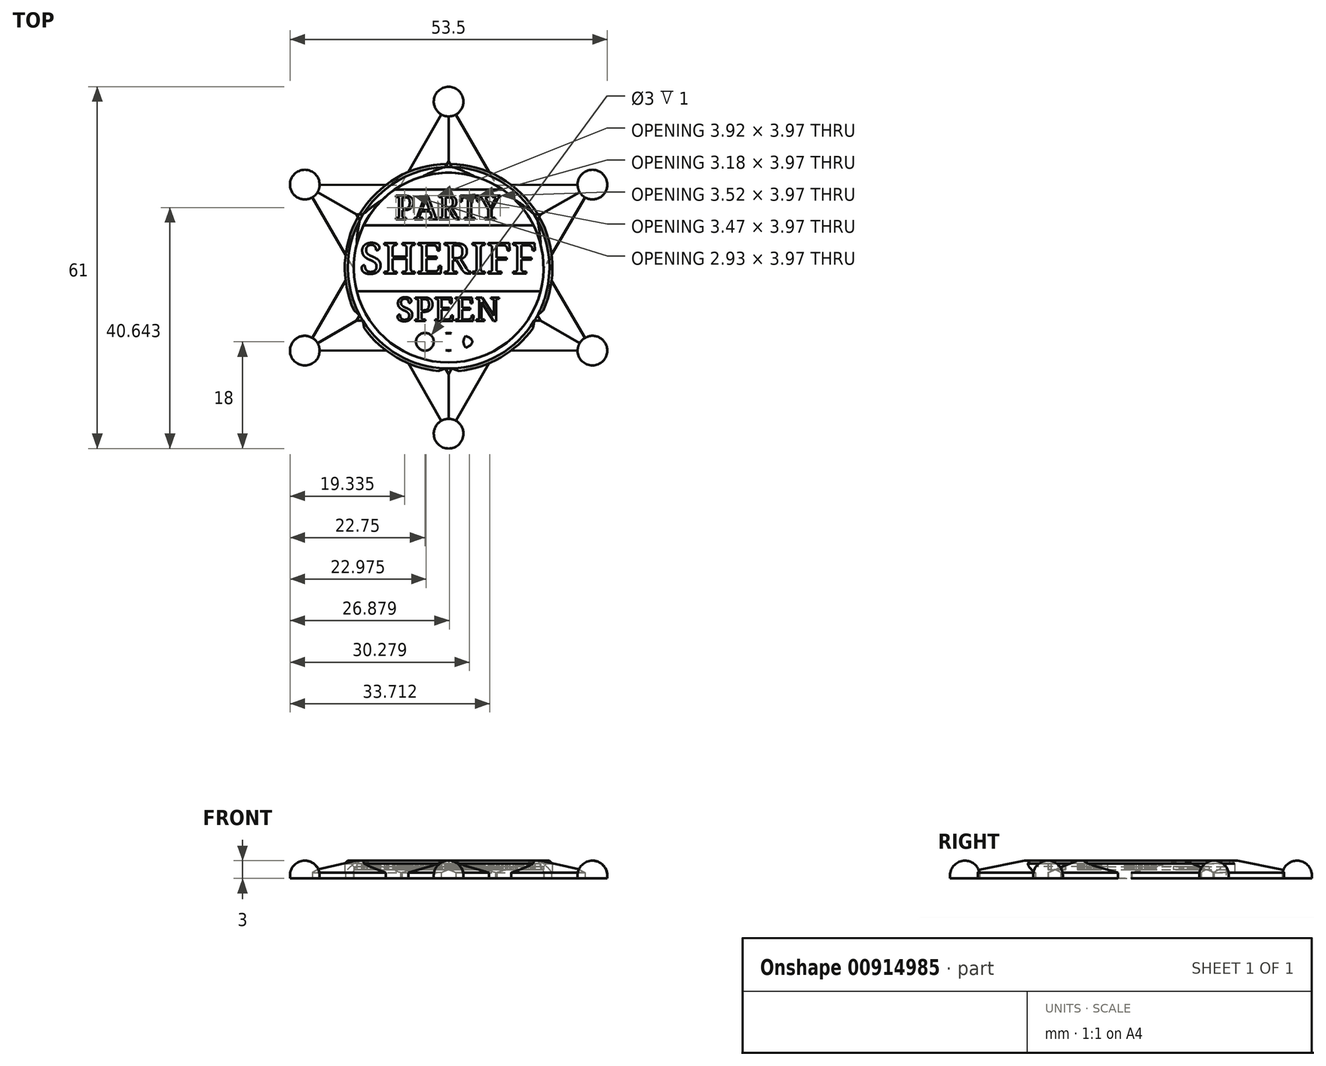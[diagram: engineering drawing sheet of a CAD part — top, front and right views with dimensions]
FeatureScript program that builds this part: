
annotation { "Feature Type Name" : "Feature", "Feature Type Description" : "" }
export const myFeature = defineFeature(function(context is Context, id is Id, definition is map)
    precondition{}
    {
        {
            var Q0;
            Q0=qCreatedBy(makeId("Top.planeOp"),FACE);
            var sketch = newSketch(context, id + "F0", { "sketchPlane" : qUnion([Q0])});
            skCircle(sketch, "E0", {"center": v(0, 0) * mm, "radius": 16 * mm});
            skCircle(sketch, "E1", {"center": v(0, 0) * mm, "radius": 17.5 * mm});
            skSolve(sketch);
        }
        {
            var Q0;
            Q0=makeQuery(id+"F0.imprint","IMPRINT",FACE,{"disambiguationData":[TD([[makeQuery(id+"F0.imprint","IMPRINT",EDGE,{"derivedFrom":sQuery(id+"F0.wireOp",EDGE,"E0")}),1.0]])]});
            var sketch = newSketch(context, id + "F1", { "sketchPlane" : qUnion([Q0])});
            skLineSegment(sketch, "E2", {"start": v(0, -28) * mm, "end": v(-16, 0) * mm});
            skLineSegment(sketch, "E3", {"start": v(-16, 0) * mm, "end": v(16, 0) * mm});
            skLineSegment(sketch, "E4", {"start": v(16, 0) * mm, "end": v(0, -28) * mm});
            skLineSegment(sketch, "E5.1.0", {"start": v(24.25, -14) * mm, "end": v(-8, -13.86) * mm});
            skLineSegment(sketch, "E5.1.1", {"start": v(8, 13.86) * mm, "end": v(24.25, -14) * mm});
            skLineSegment(sketch, "E5.1.2", {"start": v(-8, -13.86) * mm, "end": v(8, 13.86) * mm});
            skLineSegment(sketch, "E5.2.0", {"start": v(24.25, 14) * mm, "end": v(8, -13.86) * mm});
            skLineSegment(sketch, "E5.2.1", {"start": v(-8, 13.86) * mm, "end": v(24.25, 14) * mm});
            skLineSegment(sketch, "E5.2.2", {"start": v(8, -13.86) * mm, "end": v(-8, 13.86) * mm});
            skLineSegment(sketch, "E5.3.0", {"start": v(0, 28) * mm, "end": v(16, 0) * mm});
            skLineSegment(sketch, "E5.3.1", {"start": v(-16, 0) * mm, "end": v(0, 28) * mm});
            skLineSegment(sketch, "E5.3.2", {"start": v(16, 0) * mm, "end": v(-16, 0) * mm});
            skLineSegment(sketch, "E5.4.0", {"start": v(-24.25, 14) * mm, "end": v(8, 13.86) * mm});
            skLineSegment(sketch, "E5.4.1", {"start": v(-8, -13.86) * mm, "end": v(-24.25, 14) * mm});
            skLineSegment(sketch, "E5.4.2", {"start": v(8, 13.86) * mm, "end": v(-8, -13.86) * mm});
            skLineSegment(sketch, "E5.5.0", {"start": v(-24.25, -14) * mm, "end": v(-8, 13.86) * mm});
            skLineSegment(sketch, "E5.5.1", {"start": v(8, -13.86) * mm, "end": v(-24.25, -14) * mm});
            skLineSegment(sketch, "E5.5.2", {"start": v(-8, 13.86) * mm, "end": v(8, -13.86) * mm});
            skPoint(sketch, "E5.center", {"position": v(0, 0) * mm});
            skCircle(sketch, "E6", {"center": v(0, -28) * mm, "radius": 2.5 * mm});
            skCircle(sketch, "E7.1.0", {"center": v(24.25, -14) * mm, "radius": 2.5 * mm});
            skCircle(sketch, "E7.2.0", {"center": v(24.25, 14) * mm, "radius": 2.5 * mm});
            skCircle(sketch, "E7.3.0", {"center": v(0, 28) * mm, "radius": 2.5 * mm});
            skCircle(sketch, "E7.4.0", {"center": v(-24.25, 14) * mm, "radius": 2.5 * mm});
            skCircle(sketch, "E7.5.0", {"center": v(-24.25, -14) * mm, "radius": 2.5 * mm});
            skSolve(sketch);
        }
        {
            var Q0;
            {var subQ5=sQuery(id+"F1.wireOp",EDGE,"E5.2.0");var subQ6=sQuery(id+"F1.wireOp",EDGE,"E5.1.1");var subQ7=makeQuery(id+"F1.imprint","INTERSECT",VERTEX,{"derivedFrom":[subQ6,subQ5]});Q0=makeQuery(id+"F1.imprint","IMPRINT",FACE,{"disambiguationData":[TD([[makeQuery(id+"F1.imprint","IMPRINT",EDGE,{"disambiguationData":[TD([[subQ7,1.0]])],"derivedFrom":subQ6}),1.0]])]});}
            var Q1;
            Q1=makeQuery(id+"F0.imprint","IMPRINT",FACE,{"disambiguationData":[TD([[makeQuery(id+"F0.imprint","IMPRINT",EDGE,{"derivedFrom":sQuery(id+"F0.wireOp",EDGE,"E0")}),-1.0]])]});
            var Q2;
            {var subQ5=sQuery(id+"F1.wireOp",EDGE,"E5.1.0");var subQ6=sQuery(id+"F1.wireOp",EDGE,"E4");var subQ7=makeQuery(id+"F1.imprint","INTERSECT",VERTEX,{"derivedFrom":[subQ6,subQ5]});Q2=makeQuery(id+"F1.imprint","IMPRINT",FACE,{"disambiguationData":[TD([[makeQuery(id+"F1.imprint","IMPRINT",EDGE,{"disambiguationData":[TD([[subQ7,1.0]])],"derivedFrom":subQ6}),1.0]])]});}
            var Q3;
            {var subQ5=sQuery(id+"F1.wireOp",EDGE,"E6");var subQ6=sQuery(id+"F1.wireOp",EDGE,"E2");var subQ7=makeQuery(id+"F1.imprint","INTERSECT",VERTEX,{"derivedFrom":[subQ6,subQ5]});Q3=makeQuery(id+"F1.imprint","IMPRINT",FACE,{"disambiguationData":[TD([[makeQuery(id+"F1.imprint","IMPRINT",EDGE,{"disambiguationData":[TD([[subQ7,-1.0]])],"derivedFrom":subQ6}),-1.0]])]});}
            var Q4;
            {var subQ7=sQuery(id+"F1.wireOp",EDGE,"E5.3.0");var subQ8=sQuery(id+"F1.wireOp",EDGE,"E5.2.1");var subQ9=makeQuery(id+"F1.imprint","INTERSECT",VERTEX,{"derivedFrom":[subQ8,subQ7]});Q4=makeQuery(id+"F1.imprint","IMPRINT",FACE,{"disambiguationData":[TD([[makeQuery(id+"F1.imprint","IMPRINT",EDGE,{"disambiguationData":[TD([[subQ9,1.0]])],"derivedFrom":subQ8}),1.0]])]});}
            var Q5;
            {var subQ7=sQuery(id+"F1.wireOp",EDGE,"E5.5.1");var subQ8=sQuery(id+"F1.wireOp",EDGE,"E2");var subQ9=makeQuery(id+"F1.imprint","INTERSECT",VERTEX,{"derivedFrom":[subQ8,subQ7]});Q5=makeQuery(id+"F1.imprint","IMPRINT",FACE,{"disambiguationData":[TD([[makeQuery(id+"F1.imprint","IMPRINT",EDGE,{"disambiguationData":[TD([[subQ9,-1.0]])],"derivedFrom":subQ8}),1.0]])]});}
            var Q6;
            {var subQ7=sQuery(id+"F1.wireOp",EDGE,"E5.4.0");var subQ8=sQuery(id+"F1.wireOp",EDGE,"E5.3.1");var subQ9=makeQuery(id+"F1.imprint","INTERSECT",VERTEX,{"derivedFrom":[subQ8,subQ7]});Q6=makeQuery(id+"F1.imprint","IMPRINT",FACE,{"disambiguationData":[TD([[makeQuery(id+"F1.imprint","IMPRINT",EDGE,{"disambiguationData":[TD([[subQ9,1.0]])],"derivedFrom":subQ8}),1.0]])]});}
            extrude(context, id + "F2", {"entities" : qUnion([Q0, Q1, Q2, Q3, Q4, Q5, Q6]), "depth" : 3 * mm, "offsetDistance" : 25 * mm});
        }
        {
            var Q0;
            {var subQ0=sQuery(id+"F1.wireOp",EDGE,"E5.5.1");var subQ1=sQuery(id+"F1.wireOp",EDGE,"E5.5.0");var subQ2=makeQuery(id+"F1.imprint","INTERSECT",VERTEX,{"derivedFrom":[subQ1,subQ0]});Q0=makeQuery(id+"F1.imprint","IMPRINT",FACE,{"disambiguationData":[TD([[makeQuery(id+"F1.imprint","IMPRINT",EDGE,{"disambiguationData":[TD([[subQ2,-1.0]])],"derivedFrom":subQ1}),-1.0]])]});}
            var Q1;
            {var subQ0=sQuery(id+"F1.wireOp",EDGE,"E5.4.1");var subQ1=sQuery(id+"F1.wireOp",EDGE,"E5.4.0");var subQ2=makeQuery(id+"F1.imprint","INTERSECT",VERTEX,{"derivedFrom":[subQ1,subQ0]});Q1=makeQuery(id+"F1.imprint","IMPRINT",FACE,{"disambiguationData":[TD([[makeQuery(id+"F1.imprint","IMPRINT",EDGE,{"disambiguationData":[TD([[subQ2,-1.0]])],"derivedFrom":subQ1}),1.0]])]});}
            var Q2;
            {var subQ0=sQuery(id+"F1.wireOp",EDGE,"E5.3.1");var subQ1=sQuery(id+"F1.wireOp",EDGE,"E5.3.0");var subQ2=makeQuery(id+"F1.imprint","INTERSECT",VERTEX,{"derivedFrom":[subQ1,subQ0]});Q2=makeQuery(id+"F1.imprint","IMPRINT",FACE,{"disambiguationData":[TD([[makeQuery(id+"F1.imprint","IMPRINT",EDGE,{"disambiguationData":[TD([[subQ2,-1.0]])],"derivedFrom":subQ1}),-1.0]])]});}
            var Q3;
            {var subQ0=sQuery(id+"F1.wireOp",EDGE,"E5.5.1");var subQ1=sQuery(id+"F1.wireOp",EDGE,"E5.5.0");var subQ2=makeQuery(id+"F1.imprint","INTERSECT",VERTEX,{"derivedFrom":[subQ1,subQ0]});Q3=makeQuery(id+"F1.imprint","IMPRINT",FACE,{"disambiguationData":[TD([[makeQuery(id+"F1.imprint","IMPRINT",EDGE,{"disambiguationData":[TD([[subQ2,-1.0]])],"derivedFrom":subQ1}),1.0]])]});}
            var Q4;
            {var subQ0=sQuery(id+"F1.wireOp",EDGE,"E5.3.1");var subQ1=sQuery(id+"F1.wireOp",EDGE,"E5.3.0");var subQ2=makeQuery(id+"F1.imprint","INTERSECT",VERTEX,{"derivedFrom":[subQ1,subQ0]});Q4=makeQuery(id+"F1.imprint","IMPRINT",FACE,{"disambiguationData":[TD([[makeQuery(id+"F1.imprint","IMPRINT",EDGE,{"disambiguationData":[TD([[subQ2,-1.0]])],"derivedFrom":subQ1}),1.0]])]});}
            var Q5;
            {var subQ0=sQuery(id+"F1.wireOp",EDGE,"E5.2.1");var subQ1=sQuery(id+"F1.wireOp",EDGE,"E5.2.0");var subQ2=makeQuery(id+"F1.imprint","INTERSECT",VERTEX,{"derivedFrom":[subQ1,subQ0]});Q5=makeQuery(id+"F1.imprint","IMPRINT",FACE,{"disambiguationData":[TD([[makeQuery(id+"F1.imprint","IMPRINT",EDGE,{"disambiguationData":[TD([[subQ2,-1.0]])],"derivedFrom":subQ1}),-1.0]])]});}
            var Q6;
            {var subQ0=sQuery(id+"F1.wireOp",EDGE,"E5.4.1");var subQ1=sQuery(id+"F1.wireOp",EDGE,"E5.4.0");var subQ2=makeQuery(id+"F1.imprint","INTERSECT",VERTEX,{"derivedFrom":[subQ1,subQ0]});Q6=makeQuery(id+"F1.imprint","IMPRINT",FACE,{"disambiguationData":[TD([[makeQuery(id+"F1.imprint","IMPRINT",EDGE,{"disambiguationData":[TD([[subQ2,-1.0]])],"derivedFrom":subQ1}),-1.0]])]});}
            var Q7;
            {var subQ0=sQuery(id+"F1.wireOp",EDGE,"E5.2.1");var subQ1=sQuery(id+"F1.wireOp",EDGE,"E5.2.0");var subQ2=makeQuery(id+"F1.imprint","INTERSECT",VERTEX,{"derivedFrom":[subQ1,subQ0]});Q7=makeQuery(id+"F1.imprint","IMPRINT",FACE,{"disambiguationData":[TD([[makeQuery(id+"F1.imprint","IMPRINT",EDGE,{"disambiguationData":[TD([[subQ2,-1.0]])],"derivedFrom":subQ1}),1.0]])]});}
            var Q8;
            {var subQ0=sQuery(id+"F1.wireOp",EDGE,"E5.1.1");var subQ1=sQuery(id+"F1.wireOp",EDGE,"E5.1.0");var subQ2=makeQuery(id+"F1.imprint","INTERSECT",VERTEX,{"derivedFrom":[subQ1,subQ0]});Q8=makeQuery(id+"F1.imprint","IMPRINT",FACE,{"disambiguationData":[TD([[makeQuery(id+"F1.imprint","IMPRINT",EDGE,{"disambiguationData":[TD([[subQ2,-1.0]])],"derivedFrom":subQ1}),1.0]])]});}
            var Q9;
            {var subQ0=sQuery(id+"F1.wireOp",EDGE,"E5.1.1");var subQ1=sQuery(id+"F1.wireOp",EDGE,"E5.1.0");var subQ2=makeQuery(id+"F1.imprint","INTERSECT",VERTEX,{"derivedFrom":[subQ1,subQ0]});Q9=makeQuery(id+"F1.imprint","IMPRINT",FACE,{"disambiguationData":[TD([[makeQuery(id+"F1.imprint","IMPRINT",EDGE,{"disambiguationData":[TD([[subQ2,-1.0]])],"derivedFrom":subQ1}),-1.0]])]});}
            var Q10;
            {var subQ0=sQuery(id+"F1.wireOp",EDGE,"E4");var subQ1=sQuery(id+"F1.wireOp",EDGE,"E2");var subQ2=makeQuery(id+"F1.imprint","INTERSECT",VERTEX,{"derivedFrom":[subQ1,subQ0]});Q10=makeQuery(id+"F1.imprint","IMPRINT",FACE,{"disambiguationData":[TD([[makeQuery(id+"F1.imprint","IMPRINT",EDGE,{"disambiguationData":[TD([[subQ2,-1.0]])],"derivedFrom":subQ1}),-1.0]])]});}
            var Q11;
            {var subQ0=sQuery(id+"F1.wireOp",EDGE,"E4");var subQ1=sQuery(id+"F1.wireOp",EDGE,"E2");var subQ2=makeQuery(id+"F1.imprint","INTERSECT",VERTEX,{"derivedFrom":[subQ1,subQ0]});Q11=makeQuery(id+"F1.imprint","IMPRINT",FACE,{"disambiguationData":[TD([[makeQuery(id+"F1.imprint","IMPRINT",EDGE,{"disambiguationData":[TD([[subQ2,-1.0]])],"derivedFrom":subQ1}),1.0]])]});}
            extrude(context, id + "F3", {"entities" : qUnion([Q0, Q1, Q2, Q3, Q4, Q5, Q6, Q7, Q8, Q9, Q10, Q11]), "depth" : 3 * mm, "offsetDistance" : 25 * mm});
        }
        {
            var Q0;
            Q0=makeQuery(id+"F0.imprint","IMPRINT",FACE,{"disambiguationData":[TD([[makeQuery(id+"F0.imprint","IMPRINT",EDGE,{"derivedFrom":sQuery(id+"F0.wireOp",EDGE,"E0")}),1.0]])]});
            extrude(context, id + "F4", {"entities" : qUnion([Q0]), "depth" : 1.5 * mm, "offsetDistance" : 25 * mm});
        }
        {
            var Q0;
            {var subQ0=sQuery(id+"F1.wireOp",EDGE,"E5.5.0");Q0=makeQuery(id+"F2.opExtrude","CAP_EDGE",EDGE,{"disambiguationData":[OSD([subQ0]),TDD([makeQuery(id+"F1.imprint","IMPRINT",EDGE,{"disambiguationData":[TD([[makeQuery(id+"F1.imprint","INTERSECT",VERTEX,{"derivedFrom":[sQuery(id+"F1.wireOp",EDGE,"E5.4.1"),subQ0]}),1.0]])],"derivedFrom":subQ0})])],"isStart":false});}
            var Q1;
            {var subQ0=sQuery(id+"F1.wireOp",EDGE,"E5.4.0");Q1=makeQuery(id+"F2.opExtrude","CAP_EDGE",EDGE,{"disambiguationData":[OSD([subQ0]),TDD([makeQuery(id+"F1.imprint","IMPRINT",EDGE,{"disambiguationData":[TD([[makeQuery(id+"F1.imprint","INTERSECT",VERTEX,{"derivedFrom":[sQuery(id+"F1.wireOp",EDGE,"E5.3.1"),subQ0]}),1.0]])],"derivedFrom":subQ0})])],"isStart":false});}
            var Q2;
            {var subQ0=sQuery(id+"F1.wireOp",EDGE,"E5.4.1");Q2=makeQuery(id+"F2.opExtrude","CAP_EDGE",EDGE,{"disambiguationData":[OSD([subQ0]),TDD([makeQuery(id+"F1.imprint","IMPRINT",EDGE,{"disambiguationData":[TD([[makeQuery(id+"F1.imprint","INTERSECT",VERTEX,{"derivedFrom":[subQ0,sQuery(id+"F1.wireOp",EDGE,"E5.5.0")]}),-1.0]])],"derivedFrom":subQ0})])],"isStart":false});}
            var Q3;
            {var subQ0=sQuery(id+"F1.wireOp",EDGE,"E5.3.1");Q3=makeQuery(id+"F2.opExtrude","CAP_EDGE",EDGE,{"disambiguationData":[OSD([subQ0]),TDD([makeQuery(id+"F1.imprint","IMPRINT",EDGE,{"disambiguationData":[TD([[makeQuery(id+"F1.imprint","INTERSECT",VERTEX,{"derivedFrom":[subQ0,sQuery(id+"F1.wireOp",EDGE,"E5.4.0")]}),-1.0]])],"derivedFrom":subQ0})])],"isStart":false});}
            var Q4;
            {var subQ0=sQuery(id+"F1.wireOp",EDGE,"E5.3.0");Q4=makeQuery(id+"F2.opExtrude","CAP_EDGE",EDGE,{"disambiguationData":[OSD([subQ0]),TDD([makeQuery(id+"F1.imprint","IMPRINT",EDGE,{"disambiguationData":[TD([[makeQuery(id+"F1.imprint","INTERSECT",VERTEX,{"derivedFrom":[sQuery(id+"F1.wireOp",EDGE,"E5.2.1"),subQ0]}),1.0]])],"derivedFrom":subQ0})])],"isStart":false});}
            var Q5;
            {var subQ0=sQuery(id+"F1.wireOp",EDGE,"E5.2.1");Q5=makeQuery(id+"F2.opExtrude","CAP_EDGE",EDGE,{"disambiguationData":[OSD([subQ0]),TDD([makeQuery(id+"F1.imprint","IMPRINT",EDGE,{"disambiguationData":[TD([[makeQuery(id+"F1.imprint","INTERSECT",VERTEX,{"derivedFrom":[subQ0,sQuery(id+"F1.wireOp",EDGE,"E5.3.0")]}),-1.0]])],"derivedFrom":subQ0})])],"isStart":false});}
            var Q6;
            {var subQ0=sQuery(id+"F1.wireOp",EDGE,"E5.2.0");Q6=makeQuery(id+"F2.opExtrude","CAP_EDGE",EDGE,{"disambiguationData":[OSD([subQ0]),TDD([makeQuery(id+"F1.imprint","IMPRINT",EDGE,{"disambiguationData":[TD([[makeQuery(id+"F1.imprint","INTERSECT",VERTEX,{"derivedFrom":[sQuery(id+"F1.wireOp",EDGE,"E5.1.1"),subQ0]}),1.0]])],"derivedFrom":subQ0})])],"isStart":false});}
            var Q7;
            {var subQ0=sQuery(id+"F1.wireOp",EDGE,"E5.1.1");Q7=makeQuery(id+"F2.opExtrude","CAP_EDGE",EDGE,{"disambiguationData":[OSD([subQ0]),TDD([makeQuery(id+"F1.imprint","IMPRINT",EDGE,{"disambiguationData":[TD([[makeQuery(id+"F1.imprint","INTERSECT",VERTEX,{"derivedFrom":[subQ0,sQuery(id+"F1.wireOp",EDGE,"E5.2.0")]}),-1.0]])],"derivedFrom":subQ0})])],"isStart":false});}
            var Q8;
            {var subQ0=sQuery(id+"F1.wireOp",EDGE,"E5.1.0");Q8=makeQuery(id+"F2.opExtrude","CAP_EDGE",EDGE,{"disambiguationData":[OSD([subQ0]),TDD([makeQuery(id+"F1.imprint","IMPRINT",EDGE,{"disambiguationData":[TD([[makeQuery(id+"F1.imprint","INTERSECT",VERTEX,{"derivedFrom":[sQuery(id+"F1.wireOp",EDGE,"E4"),subQ0]}),1.0]])],"derivedFrom":subQ0})])],"isStart":false});}
            var Q9;
            {var subQ0=sQuery(id+"F1.wireOp",EDGE,"E4");Q9=makeQuery(id+"F2.opExtrude","CAP_EDGE",EDGE,{"disambiguationData":[OSD([subQ0]),TDD([makeQuery(id+"F1.imprint","IMPRINT",EDGE,{"disambiguationData":[TD([[makeQuery(id+"F1.imprint","INTERSECT",VERTEX,{"derivedFrom":[subQ0,sQuery(id+"F1.wireOp",EDGE,"E5.1.0")]}),-1.0]])],"derivedFrom":subQ0})])],"isStart":false});}
            var Q10;
            {var subQ0=sQuery(id+"F1.wireOp",EDGE,"E2");Q10=makeQuery(id+"F2.opExtrude","CAP_EDGE",EDGE,{"disambiguationData":[OSD([subQ0]),TDD([makeQuery(id+"F1.imprint","IMPRINT",EDGE,{"disambiguationData":[TD([[makeQuery(id+"F1.imprint","INTERSECT",VERTEX,{"derivedFrom":[subQ0,sQuery(id+"F1.wireOp",EDGE,"E6")]}),-1.0]])],"derivedFrom":subQ0})])],"isStart":false});}
            var Q11;
            {var subQ0=sQuery(id+"F1.wireOp",EDGE,"E5.5.1");Q11=makeQuery(id+"F2.opExtrude","CAP_EDGE",EDGE,{"disambiguationData":[OSD([subQ0]),TDD([makeQuery(id+"F1.imprint","IMPRINT",EDGE,{"disambiguationData":[TD([[makeQuery(id+"F1.imprint","INTERSECT",VERTEX,{"derivedFrom":[sQuery(id+"F1.wireOp",EDGE,"E2"),subQ0]}),-1.0]])],"derivedFrom":subQ0})])],"isStart":false});}
            chamfer(context, id + "F5", {"entities" : qUnion([Q0, Q1, Q2, Q3, Q4, Q5, Q6, Q7, Q8, Q9, Q10, Q11]), "chamferType" : ChamferType.TWO_OFFSETS, "width1" : 2 * mm, "oppositeDirection" : false, "width2" : 5 * mm, "tangentPropagation" : true});
        }
        {
            var Q0;
            Q0=makeQuery(id+"F3.opExtrude","CAP_EDGE",EDGE,{"disambiguationData":[OSD([sQuery(id+"F1.wireOp",EDGE,"E7.5.0")])],"isStart":false});
            var Q1;
            Q1=makeQuery(id+"F3.opExtrude","CAP_EDGE",EDGE,{"disambiguationData":[OSD([sQuery(id+"F1.wireOp",EDGE,"E7.4.0")])],"isStart":false});
            var Q2;
            Q2=makeQuery(id+"F3.opExtrude","CAP_EDGE",EDGE,{"disambiguationData":[OSD([sQuery(id+"F1.wireOp",EDGE,"E6")])],"isStart":false});
            var Q3;
            Q3=makeQuery(id+"F3.opExtrude","CAP_EDGE",EDGE,{"disambiguationData":[OSD([sQuery(id+"F1.wireOp",EDGE,"E7.2.0")])],"isStart":false});
            var Q4;
            Q4=makeQuery(id+"F3.opExtrude","CAP_EDGE",EDGE,{"disambiguationData":[OSD([sQuery(id+"F1.wireOp",EDGE,"E7.1.0")])],"isStart":false});
            var Q5;
            Q5=makeQuery(id+"F3.opExtrude","CAP_EDGE",EDGE,{"disambiguationData":[OSD([sQuery(id+"F1.wireOp",EDGE,"E7.3.0")])],"isStart":false});
            fillet(context, id + "F6", {"entities" : qUnion([Q0, Q1, Q2, Q3, Q4, Q5]), "radius" : 2.5 * mm, "tangentPropagation" : true, "allowEdgeOverflow" : false});
        }
        {
            var Q0;
            Q0=makeQuery(id+"F2.opExtrude","CAP_EDGE",EDGE,{"disambiguationData":[OSD([sQuery(id+"F0.wireOp",EDGE,"E1")])],"isStart":false});
            chamfer(context, id + "F7", {"entities" : qUnion([Q0]), "width" : .5 * mm, "tangentPropagation" : true});
        }
        {
            var Q0;
            Q0=makeQuery(id+"F4.opExtrude","CAP_FACE",FACE,{"disambiguationData":[OSD([sQuery(id+"F0.wireOp",EDGE,"E0")])],"isStart":false});
            var sketch = newSketch(context, id + "F8", { "sketchPlane" : qUnion([Q0])});
            skText(sketch, "E8", { "text": "SHERIFF", "fontName": "NotoSerif-Regular.ttf"});
            skText(sketch, "E9", { "text": "SPEEN", "fontName": "NotoSerif-Regular.ttf"});
            skText(sketch, "E10", { "text": "PARTY", "fontName": "NotoSerif-Regular.ttf"});
            skLineSegment(sketch, "E11", {"start": v(-9.1, 13.16) * mm, "end": v(9.1, 13.16) * mm});
            skLineSegment(sketch, "E12", {"start": v(-14.3, 7.16) * mm, "end": v(14.3, 7.16) * mm});
            skLineSegment(sketch, "E13", {"start": v(-15.5, -4) * mm, "end": v(15.5, -4) * mm});
            skLineSegment(sketch, "E14", {"start": v(-9.99, -12.5) * mm, "end": v(9.99, -12.5) * mm});
            skLineSegment(sketch, "E15", {"start": v(0, -9) * mm, "end": v(0, -12.5) * mm, "construction": true});
            skLineSegment(sketch, "E16", {"start": v(0, -12.5) * mm, "end": v(0, -16) * mm, "construction": true});
            skCircle(sketch, "E17", {"center": v(0, -12.5) * mm, "radius": 1.5 * mm});
            skCircle(sketch, "E18", {"center": v(4, -12.5) * mm, "radius": 1.5 * mm});
            skCircle(sketch, "E19", {"center": v(-4, -12.5) * mm, "radius": 1.5 * mm});
            skEllipse(sketch, "E20", {"center": v(0, -12.5) * mm, "majorRadius": 4 * mm, "minorRadius": 1.43 * mm, "majorAxis": v(-1, 0)});
            const initialGuessF8  = {"E8": [-0.015, -0.001, 1, 0, 0.00516], "E9": [-0.00887, -0.009, 1, 0, 0.004], "E10": [-0.00909, 0.00816, 1, 0, 0.004]};
            skSetInitialGuess(sketch, initialGuessF8);
            skSolve(sketch);
        }
        {
            var Q0;
            Q0=makeQuery(id+"F8.imprint","IMPRINT",FACE,{"disambiguationData":[TD([[makeQuery(id+"F8.imprint","IMPRINT",EDGE,{"derivedFrom":sQuery(id+"F8.wireOp",EDGE,"E10.sketch_text.stroke-0")}),1.0]])]});
            var Q1;
            Q1=makeQuery(id+"F8.imprint","IMPRINT",FACE,{"disambiguationData":[TD([[makeQuery(id+"F8.imprint","IMPRINT",EDGE,{"derivedFrom":sQuery(id+"F8.wireOp",EDGE,"E10.sketch_text.stroke-122")}),1.0]])]});
            var Q2;
            Q2=makeQuery(id+"F8.imprint","IMPRINT",FACE,{"disambiguationData":[TD([[makeQuery(id+"F8.imprint","IMPRINT",EDGE,{"derivedFrom":sQuery(id+"F8.wireOp",EDGE,"E10.sketch_text.stroke-73")}),1.0]])]});
            var Q3;
            Q3=makeQuery(id+"F8.imprint","IMPRINT",FACE,{"disambiguationData":[TD([[makeQuery(id+"F8.imprint","IMPRINT",EDGE,{"derivedFrom":sQuery(id+"F8.wireOp",EDGE,"E10.sketch_text.stroke-31")}),1.0]])]});
            var Q4;
            Q4=makeQuery(id+"F8.imprint","IMPRINT",FACE,{"disambiguationData":[TD([[makeQuery(id+"F8.imprint","IMPRINT",EDGE,{"derivedFrom":sQuery(id+"F8.wireOp",EDGE,"E9.sketch_text.stroke-0")}),1.0]])]});
            var Q5;
            Q5=makeQuery(id+"F8.imprint","IMPRINT",FACE,{"disambiguationData":[TD([[makeQuery(id+"F8.imprint","IMPRINT",EDGE,{"derivedFrom":sQuery(id+"F8.wireOp",EDGE,"E9.sketch_text.stroke-81")}),1.0]])]});
            extrude(context, id + "F9", {"entities" : qUnion([Q0, Q1, Q2, Q3, Q4, Q5]), "depth" : .5 * mm, "offsetDistance" : 25 * mm});
        }
        {
            var Q0;
            {var subQ0=sQuery(id+"F0.wireOp",EDGE,"E0");Q0=makeQuery(id+"F2.opExtrude","CAP_EDGE",EDGE,{"disambiguationData":[OSD([subQ0]),TDD([makeQuery(id+"F0.imprint","IMPRINT",EDGE,{"derivedFrom":subQ0})])],"isStart":false});}
            chamfer(context, id + "F10", {"entities" : qUnion([Q0]), "width" : 1 * mm, "tangentPropagation" : true});
        }
        {
            var Q0;
            {var subQ0=sQuery(id+"F0.wireOp",EDGE,"E0");var subQ1=makeQuery(id+"F0.imprint","IMPRINT",EDGE,{"derivedFrom":subQ0});Q0=makeQuery(id+"F2.opExtrude","CAP_EDGE",EDGE,{"disambiguationData":[OSD([subQ0]),TDD([makeQuery(id+"F1.imprint","IMPRINT",EDGE,{"disambiguationData":[TD([[makeQuery(id+"F1.imprint","INTERSECT",VERTEX,{"derivedFrom":[subQ1,sQuery(id+"F1.wireOp",EDGE,"E5.2.1")]}),-1.0]])],"derivedFrom":subQ1})])],"isStart":false});}
            var Q1;
            {var subQ0=sQuery(id+"F0.wireOp",EDGE,"E0");var subQ1=makeQuery(id+"F0.imprint","IMPRINT",EDGE,{"derivedFrom":subQ0});Q1=makeQuery(id+"F2.opExtrude","CAP_EDGE",EDGE,{"disambiguationData":[OSD([subQ0]),TDD([makeQuery(id+"F1.imprint","IMPRINT",EDGE,{"disambiguationData":[TD([[makeQuery(id+"F1.imprint","INTERSECT",VERTEX,{"derivedFrom":[subQ1,sQuery(id+"F1.wireOp",EDGE,"E5.1.1")]}),-1.0]])],"derivedFrom":subQ1})])],"isStart":false});}
            var Q2;
            {var subQ0=sQuery(id+"F0.wireOp",EDGE,"E0");var subQ1=makeQuery(id+"F0.imprint","IMPRINT",EDGE,{"derivedFrom":subQ0});Q2=makeQuery(id+"F2.opExtrude","CAP_EDGE",EDGE,{"disambiguationData":[OSD([subQ0]),TDD([makeQuery(id+"F1.imprint","IMPRINT",EDGE,{"disambiguationData":[TD([[makeQuery(id+"F1.imprint","INTERSECT",VERTEX,{"derivedFrom":[subQ1,sQuery(id+"F1.wireOp",EDGE,"E2")]}),1.0]])],"derivedFrom":subQ1})])],"isStart":false});}
            var Q3;
            {var subQ0=sQuery(id+"F0.wireOp",EDGE,"E0");var subQ1=makeQuery(id+"F0.imprint","IMPRINT",EDGE,{"derivedFrom":subQ0});Q3=makeQuery(id+"F2.opExtrude","CAP_EDGE",EDGE,{"disambiguationData":[OSD([subQ0]),TDD([makeQuery(id+"F1.imprint","IMPRINT",EDGE,{"disambiguationData":[TD([[makeQuery(id+"F1.imprint","INTERSECT",VERTEX,{"derivedFrom":[subQ1,sQuery(id+"F1.wireOp",EDGE,"E4")]}),-1.0]])],"derivedFrom":subQ1})])],"isStart":false});}
            var Q4;
            {var subQ0=sQuery(id+"F0.wireOp",EDGE,"E0");var subQ1=makeQuery(id+"F0.imprint","IMPRINT",EDGE,{"derivedFrom":subQ0});Q4=makeQuery(id+"F2.opExtrude","CAP_EDGE",EDGE,{"disambiguationData":[OSD([subQ0]),TDD([makeQuery(id+"F1.imprint","IMPRINT",EDGE,{"disambiguationData":[TD([[makeQuery(id+"F1.imprint","INTERSECT",VERTEX,{"derivedFrom":[subQ1,sQuery(id+"F1.wireOp",EDGE,"E5.1.0")]}),1.0]])],"derivedFrom":subQ1})])],"isStart":false});}
            var Q5;
            {var subQ0=sQuery(id+"F0.wireOp",EDGE,"E0");var subQ1=makeQuery(id+"F0.imprint","IMPRINT",EDGE,{"derivedFrom":subQ0});Q5=makeQuery(id+"F2.opExtrude","CAP_EDGE",EDGE,{"disambiguationData":[OSD([subQ0]),TDD([makeQuery(id+"F1.imprint","IMPRINT",EDGE,{"disambiguationData":[TD([[makeQuery(id+"F1.imprint","INTERSECT",VERTEX,{"derivedFrom":[subQ1,sQuery(id+"F1.wireOp",EDGE,"E5.3.1")]}),-1.0]])],"derivedFrom":subQ1})])],"isStart":false});}
            chamfer(context, id + "F11", {"entities" : qUnion([Q0, Q1, Q2, Q3, Q4, Q5]), "width" : 1 * mm, "tangentPropagation" : true});
        }
        {
            var Q0;
            Q0=makeQuery(id+"F8.imprint","IMPRINT",FACE,{"disambiguationData":[TD([[makeQuery(id+"F8.imprint","IMPRINT",EDGE,{"derivedFrom":sQuery(id+"F8.wireOp",EDGE,"E8.sketch_text.stroke-225")}),-1.0]])]});
            var Q1;
            Q1=makeQuery(id+"F8.imprint","IMPRINT",FACE,{"disambiguationData":[TD([[makeQuery(id+"F8.imprint","IMPRINT",EDGE,{"derivedFrom":sQuery(id+"F8.wireOp",EDGE,"E8.sketch_text.stroke-0")}),-1.0]])]});
            var Q2;
            Q2=makeQuery(id+"F8.imprint","IMPRINT",FACE,{"disambiguationData":[TD([[makeQuery(id+"F8.imprint","IMPRINT",EDGE,{"derivedFrom":sQuery(id+"F8.wireOp",EDGE,"E8.sketch_text.stroke-50")}),-1.0]])]});
            var Q3;
            Q3=makeQuery(id+"F8.imprint","IMPRINT",FACE,{"disambiguationData":[TD([[makeQuery(id+"F8.imprint","IMPRINT",EDGE,{"derivedFrom":sQuery(id+"F8.wireOp",EDGE,"E8.sketch_text.stroke-197")}),-1.0]])]});
            var Q4;
            Q4=makeQuery(id+"F8.imprint","IMPRINT",FACE,{"disambiguationData":[TD([[makeQuery(id+"F8.imprint","IMPRINT",EDGE,{"derivedFrom":sQuery(id+"F8.wireOp",EDGE,"E8.sketch_text.stroke-259")}),-1.0]])]});
            var Q5;
            Q5=makeQuery(id+"F8.imprint","IMPRINT",FACE,{"disambiguationData":[TD([[makeQuery(id+"F8.imprint","IMPRINT",EDGE,{"derivedFrom":sQuery(id+"F8.wireOp",EDGE,"E8.sketch_text.stroke-110")}),-1.0]])]});
            var Q6;
            Q6=makeQuery(id+"F8.imprint","IMPRINT",FACE,{"disambiguationData":[TD([[makeQuery(id+"F8.imprint","IMPRINT",EDGE,{"derivedFrom":sQuery(id+"F8.wireOp",EDGE,"E8.sketch_text.stroke-146")}),-1.0]])]});
            var Q7;
            {var subQ0=sQuery(id+"F8.wireOp",EDGE,"E19");var subQ1=sQuery(id+"F8.wireOp",EDGE,"E14");var subQ2=makeQuery(id+"F8.imprint","INTERSECT",VERTEX,{"disambiguationData":[OD(1.0)],"derivedFrom":[subQ1,subQ0]});Q7=makeQuery(id+"F8.imprint","IMPRINT",FACE,{"disambiguationData":[TD([[makeQuery(id+"F8.imprint","IMPRINT",EDGE,{"disambiguationData":[TD([[subQ2,-1.0]])],"derivedFrom":subQ1}),-1.0]])]});}
            var Q8;
            {var subQ0=sQuery(id+"F8.wireOp",EDGE,"E19");var subQ1=sQuery(id+"F8.wireOp",EDGE,"E14");var subQ2=makeQuery(id+"F8.imprint","INTERSECT",VERTEX,{"disambiguationData":[OD(1.0)],"derivedFrom":[subQ1,subQ0]});Q8=makeQuery(id+"F8.imprint","IMPRINT",FACE,{"disambiguationData":[TD([[makeQuery(id+"F8.imprint","IMPRINT",EDGE,{"disambiguationData":[TD([[subQ2,-1.0]])],"derivedFrom":subQ1}),1.0]])]});}
            var Q9;
            {var subQ0=sQuery(id+"F8.wireOp",EDGE,"E17");var subQ1=sQuery(id+"F8.wireOp",EDGE,"E14");var subQ2=makeQuery(id+"F8.imprint","INTERSECT",VERTEX,{"disambiguationData":[OD(0.0)],"derivedFrom":[subQ1,subQ0]});Q9=makeQuery(id+"F8.imprint","IMPRINT",FACE,{"disambiguationData":[TD([[makeQuery(id+"F8.imprint","IMPRINT",EDGE,{"disambiguationData":[TD([[subQ2,-1.0]])],"derivedFrom":subQ1}),1.0]])]});}
            var Q10;
            {var subQ0=sQuery(id+"F8.wireOp",EDGE,"E17");var subQ1=sQuery(id+"F8.wireOp",EDGE,"E14");var subQ2=makeQuery(id+"F8.imprint","INTERSECT",VERTEX,{"disambiguationData":[OD(0.0)],"derivedFrom":[subQ1,subQ0]});Q10=makeQuery(id+"F8.imprint","IMPRINT",FACE,{"disambiguationData":[TD([[makeQuery(id+"F8.imprint","IMPRINT",EDGE,{"disambiguationData":[TD([[subQ2,-1.0]])],"derivedFrom":subQ1}),-1.0]])]});}
            var Q11;
            {var subQ0=sQuery(id+"F8.wireOp",EDGE,"E17");var subQ1=sQuery(id+"F8.wireOp",EDGE,"E14");var subQ2=makeQuery(id+"F8.imprint","INTERSECT",VERTEX,{"disambiguationData":[OD(1.0)],"derivedFrom":[subQ1,subQ0]});Q11=makeQuery(id+"F8.imprint","IMPRINT",FACE,{"disambiguationData":[TD([[makeQuery(id+"F8.imprint","IMPRINT",EDGE,{"disambiguationData":[TD([[subQ2,-1.0]])],"derivedFrom":subQ1}),-1.0]])]});}
            var Q12;
            {var subQ0=sQuery(id+"F8.wireOp",EDGE,"E17");var subQ1=sQuery(id+"F8.wireOp",EDGE,"E14");var subQ2=makeQuery(id+"F8.imprint","INTERSECT",VERTEX,{"disambiguationData":[OD(1.0)],"derivedFrom":[subQ1,subQ0]});Q12=makeQuery(id+"F8.imprint","IMPRINT",FACE,{"disambiguationData":[TD([[makeQuery(id+"F8.imprint","IMPRINT",EDGE,{"disambiguationData":[TD([[subQ2,-1.0]])],"derivedFrom":subQ1}),1.0]])]});}
            var Q13;
            {var subQ0=sQuery(id+"F8.wireOp",EDGE,"E20");var subQ1=sQuery(id+"F8.wireOp",EDGE,"E14");var subQ2=makeQuery(id+"F8.imprint","INTERSECT",VERTEX,{"disambiguationData":[OD(0.0)],"derivedFrom":[subQ1,subQ0]});Q13=makeQuery(id+"F8.imprint","IMPRINT",FACE,{"disambiguationData":[TD([[makeQuery(id+"F8.imprint","IMPRINT",EDGE,{"disambiguationData":[TD([[subQ2,-1.0]])],"derivedFrom":subQ1}),-1.0]])]});}
            var Q14;
            {var subQ0=sQuery(id+"F8.wireOp",EDGE,"E20");var subQ1=sQuery(id+"F8.wireOp",EDGE,"E14");var subQ2=makeQuery(id+"F8.imprint","INTERSECT",VERTEX,{"disambiguationData":[OD(0.0)],"derivedFrom":[subQ1,subQ0]});Q14=makeQuery(id+"F8.imprint","IMPRINT",FACE,{"disambiguationData":[TD([[makeQuery(id+"F8.imprint","IMPRINT",EDGE,{"disambiguationData":[TD([[subQ2,-1.0]])],"derivedFrom":subQ1}),1.0]])]});}
            var Q15;
            {var subQ0=sQuery(id+"F8.wireOp",EDGE,"E18");var subQ1=sQuery(id+"F8.wireOp",EDGE,"E14");var subQ2=makeQuery(id+"F8.imprint","INTERSECT",VERTEX,{"disambiguationData":[OD(0.0)],"derivedFrom":[subQ1,subQ0]});Q15=makeQuery(id+"F8.imprint","IMPRINT",FACE,{"disambiguationData":[TD([[makeQuery(id+"F8.imprint","IMPRINT",EDGE,{"disambiguationData":[TD([[subQ2,-1.0]])],"derivedFrom":subQ1}),-1.0]])]});}
            var Q16;
            {var subQ0=sQuery(id+"F8.wireOp",EDGE,"E18");var subQ1=sQuery(id+"F8.wireOp",EDGE,"E14");var subQ2=makeQuery(id+"F8.imprint","INTERSECT",VERTEX,{"disambiguationData":[OD(0.0)],"derivedFrom":[subQ1,subQ0]});Q16=makeQuery(id+"F8.imprint","IMPRINT",FACE,{"disambiguationData":[TD([[makeQuery(id+"F8.imprint","IMPRINT",EDGE,{"disambiguationData":[TD([[subQ2,-1.0]])],"derivedFrom":subQ1}),1.0]])]});}
            extrude(context, id + "F12", {"entities" : qUnion([Q0, Q1, Q2, Q3, Q4, Q5, Q6, Q7, Q8, Q9, Q10, Q11, Q12, Q13, Q14, Q15, Q16]), "operationType" : NewBodyOperationType.ADD, "depth" : 1 * mm, "offsetDistance" : 25 * mm});
        }
    });
